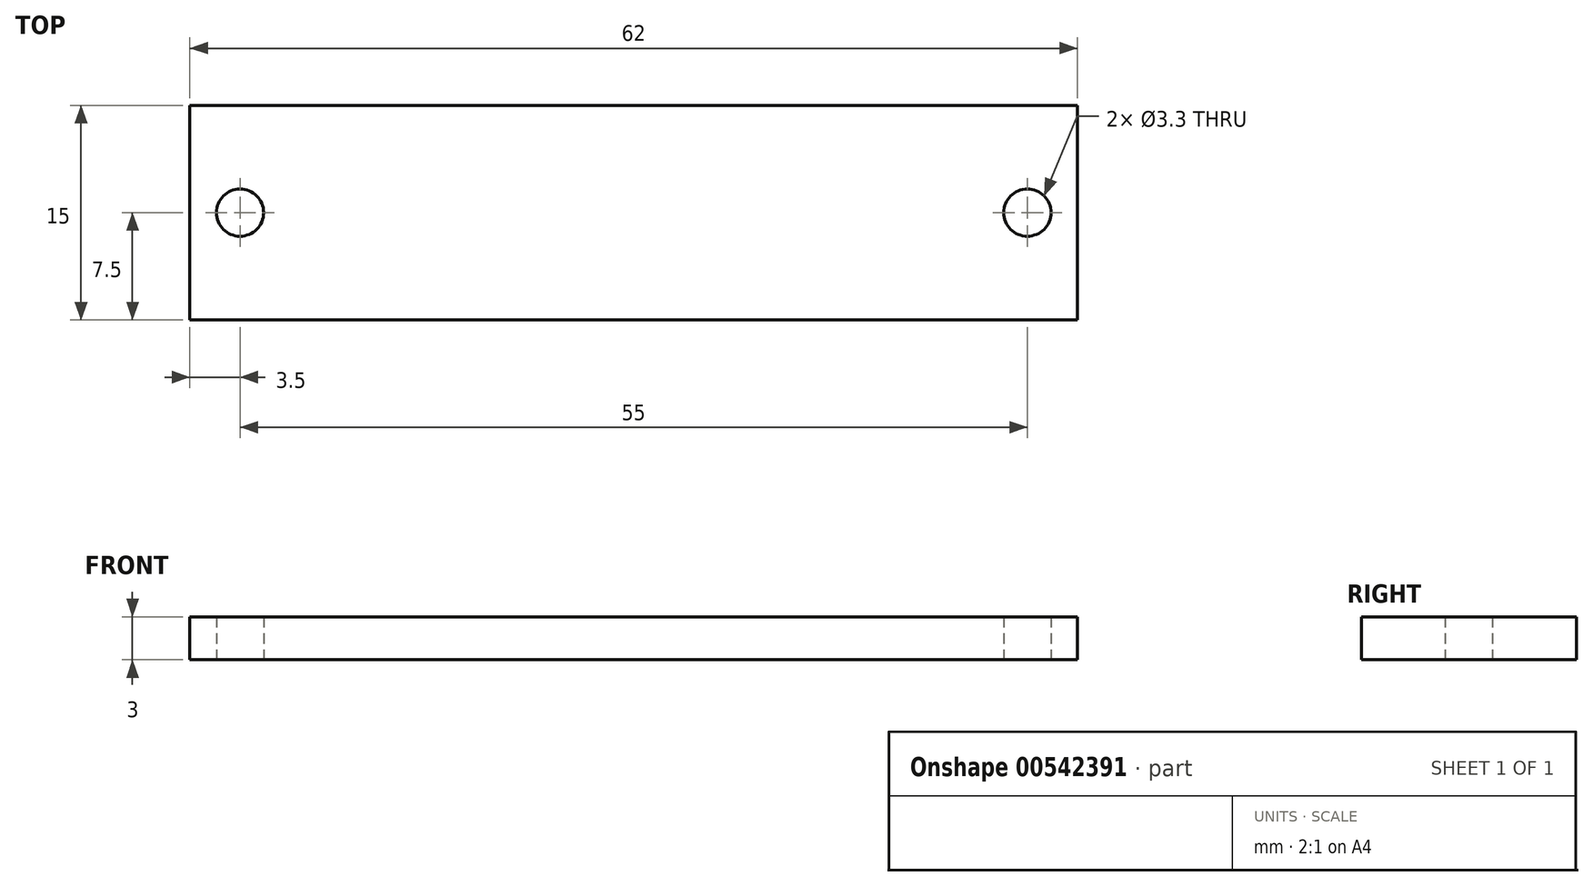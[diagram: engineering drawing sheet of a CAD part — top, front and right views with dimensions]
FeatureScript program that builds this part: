
annotation { "Feature Type Name" : "Feature", "Feature Type Description" : "" }
export const myFeature = defineFeature(function(context is Context, id is Id, definition is map)
    precondition{}
    {
        {
            var Q0;
            Q0=qCreatedBy(makeId("Top.planeOp"),FACE);
            var sketch = newSketch(context, id + "F0", { "sketchPlane" : qUnion([Q0])});
            skLineSegment(sketch, "E0.bottom", {"start": v(31, -7.5) * mm, "end": v(-31, -7.5) * mm});
            skLineSegment(sketch, "E0.top", {"start": v(31, 7.5) * mm, "end": v(-31, 7.5) * mm});
            skLineSegment(sketch, "E0.left", {"start": v(31, -7.5) * mm, "end": v(31, 7.5) * mm});
            skLineSegment(sketch, "E0.right", {"start": v(-31, -7.5) * mm, "end": v(-31, 7.5) * mm});
            skPoint(sketch, "E0.middle", {"position": v(0, 0) * mm});
            skCircle(sketch, "E1", {"center": v(-27.5, 0) * mm, "radius": 1.65 * mm});
            skCircle(sketch, "E2", {"center": v(27.5, 0) * mm, "radius": 1.65 * mm});
            skSolve(sketch);
        }
        {
            var Q0;
            Q0=makeQuery(id+"F0.imprint","IMPRINT",FACE,{"disambiguationData":[TD([[makeQuery(id+"F0.imprint","IMPRINT",EDGE,{"derivedFrom":sQuery(id+"F0.wireOp",EDGE,"E0.bottom")}),-1.0]])]});
            extrude(context, id + "F1", {"entities" : qUnion([Q0]), "depth" : 3 * mm, "offsetDistance" : 25 * mm});
        }
    });
